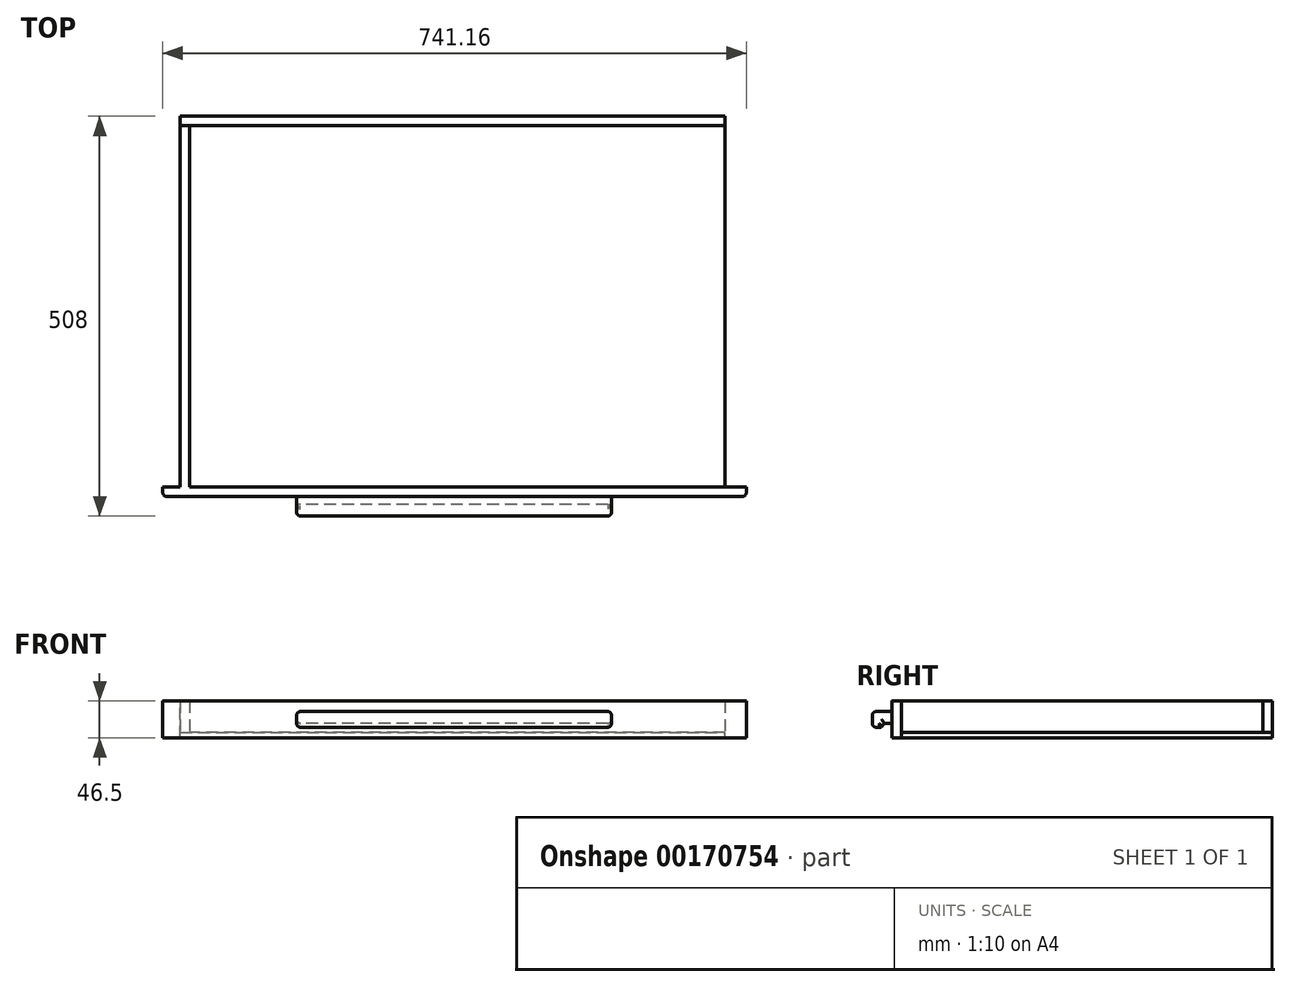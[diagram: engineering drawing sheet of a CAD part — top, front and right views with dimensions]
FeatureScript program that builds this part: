
annotation { "Feature Type Name" : "Feature", "Feature Type Description" : "" }
export const myFeature = defineFeature(function(context is Context, id is Id, definition is map)
    precondition{}
    {
        {
            assignVariable(context, id + "F0", {"name" : "height", "anyValue" : 50});
        }
        {
            var Q0;
            Q0=qCreatedBy(makeId("Top.planeOp"),FACE);
            var sketch = newSketch(context, id + "F1", { "sketchPlane" : qUnion([Q0])});
            skLineSegment(sketch, "E0.bottom", {"start": v(370, -278.25) * mm, "end": v(-370, -278.25) * mm});
            skLineSegment(sketch, "E0.top", {"start": v(370, 209.75) * mm, "end": v(-370, 209.75) * mm});
            skLineSegment(sketch, "E0.left", {"start": v(370, -278.25) * mm, "end": v(370, 209.75) * mm});
            skLineSegment(sketch, "E0.right", {"start": v(-370, -278.25) * mm, "end": v(-370, 209.75) * mm});
            skPoint(sketch, "E0.middle", {"position": v(0, -34.25) * mm});
            skLineSegment(sketch, "E1", {"start": v(-370, 197.75) * mm, "end": v(370, 197.75) * mm});
            skLineSegment(sketch, "E2", {"start": v(-358, 197.75) * mm, "end": v(-358, -278.25) * mm});
            skLineSegment(sketch, "E3.MirrorCS", {"start": v(354.04, 209.75) * mm, "end": v(354.04, -278.25) * mm});
            skLineSegment(sketch, "E4.bottom", {"start": v(-348, -278.25) * mm, "end": v(344.04, -278.25) * mm});
            skLineSegment(sketch, "E4.top", {"start": v(-348, 192.75) * mm, "end": v(344.04, 192.75) * mm});
            skLineSegment(sketch, "E4.left", {"start": v(-348, -278.25) * mm, "end": v(-348, 192.75) * mm});
            skLineSegment(sketch, "E4.right", {"start": v(344.04, -278.25) * mm, "end": v(344.04, 192.75) * mm});
            skLineSegment(sketch, "E5", {"start": v(-348, 180.75) * mm, "end": v(344.04, 180.75) * mm});
            skLineSegment(sketch, "E6", {"start": v(-336, 180.75) * mm, "end": v(-336, -278.25) * mm});
            skLineSegment(sketch, "E7", {"start": v(332.04, 180.75) * mm, "end": v(332.04, -278.25) * mm});
            skLineSegment(sketch, "E8.bottom", {"start": v(-370, -278.25) * mm, "end": v(371.16, -278.25) * mm});
            skLineSegment(sketch, "E8.top", {"start": v(-370, -290.25) * mm, "end": v(371.16, -290.25) * mm});
            skLineSegment(sketch, "E8.left", {"start": v(-370, -278.25) * mm, "end": v(-370, -290.25) * mm});
            skLineSegment(sketch, "E8.right", {"start": v(371.16, -278.25) * mm, "end": v(371.16, -290.25) * mm});
            skSolve(sketch);
        }
        {
            var Q0;
            {var subQ5=sQuery(id+"F1.wireOp",EDGE,"E6");Q0=makeQuery(id+"F1.imprint","IMPRINT",FACE,{"disambiguationData":[TD([[makeQuery(id+"F1.imprint","IMPRINT",EDGE,{"derivedFrom":subQ5}),-1.0]])]});}
            var Q1;
            {var subQ5=sQuery(id+"F1.wireOp",EDGE,"E4.top");Q1=makeQuery(id+"F1.imprint","IMPRINT",FACE,{"disambiguationData":[TD([[makeQuery(id+"F1.imprint","IMPRINT",EDGE,{"derivedFrom":subQ5}),-1.0]])]});}
            var Q2;
            {var subQ0=sQuery(id+"F1.wireOp",EDGE,"E6");Q2=makeQuery(id+"F1.imprint","IMPRINT",FACE,{"disambiguationData":[TD([[makeQuery(id+"F1.imprint","IMPRINT",EDGE,{"derivedFrom":subQ0}),1.0]])]});}
            var Q3;
            {var subQ5=sQuery(id+"F1.wireOp",EDGE,"E7");Q3=makeQuery(id+"F1.imprint","IMPRINT",FACE,{"disambiguationData":[TD([[makeQuery(id+"F1.imprint","IMPRINT",EDGE,{"derivedFrom":subQ5}),1.0]])]});}
            extrude(context, id + "F2", {"entities" : qUnion([Q0, Q1, Q2, Q3]), "oppositeDirection" : true, "depth" : 6.5 * mm});
        }
        {
            var Q0;
            {var subQ5=sQuery(id+"F1.wireOp",EDGE,"E6");Q0=makeQuery(id+"F1.imprint","IMPRINT",FACE,{"disambiguationData":[TD([[makeQuery(id+"F1.imprint","IMPRINT",EDGE,{"derivedFrom":subQ5}),-1.0]])]});}
            extrude(context, id + "F3", {"entities" : qUnion([Q0]), "depth" : (getVariable(context, 'height') - 10) * mm});
        }
        {
            var Q0;
            {var subQ5=sQuery(id+"F1.wireOp",EDGE,"E4.top");Q0=makeQuery(id+"F1.imprint","IMPRINT",FACE,{"disambiguationData":[TD([[makeQuery(id+"F1.imprint","IMPRINT",EDGE,{"derivedFrom":subQ5}),-1.0]])]});}
            var Q1;
            Q1=makeQuery(id+"F3.opExtrude","CAP_FACE",FACE,{"disambiguationData":[OSD([sQuery(id+"F1.wireOp",EDGE,"E4.left"),sQuery(id+"F1.wireOp",EDGE,"E5"),sQuery(id+"F1.wireOp",EDGE,"E6"),sQuery(id+"F1.wireOp",EDGE,"E8.bottom")])],"isStart":false});
            extrude(context, id + "F4", {"entities" : qUnion([Q0]), "endBound" : BoundingType.UP_TO_SURFACE, "endBoundEntityFace" : qUnion([Q1]), "depth" : 25 * mm});
        }
        {
            var Q0;
            Q0=makeQuery(id+"F1.imprint","IMPRINT",FACE,{"disambiguationData":[TD([[makeQuery(id+"F1.imprint","IMPRINT",EDGE,{"derivedFrom":sQuery(id+"F1.wireOp",EDGE,"E8.top")}),1.0]])]});
            var Q1;
            Q1=makeQuery(id+"F3.opExtrude","CAP_FACE",FACE,{"disambiguationData":[OSD([sQuery(id+"F1.wireOp",EDGE,"E4.left"),sQuery(id+"F1.wireOp",EDGE,"E5"),sQuery(id+"F1.wireOp",EDGE,"E6"),sQuery(id+"F1.wireOp",EDGE,"E8.bottom")])],"isStart":false});
            extrude(context, id + "F5", {"entities" : qUnion([Q0]), "endBound" : BoundingType.UP_TO_SURFACE, "endBoundEntityFace" : qUnion([Q1]), "depth" : 25 * mm});
        }
        {
            var Q0;
            Q0=makeQuery(id+"F1.imprint","IMPRINT",FACE,{"disambiguationData":[TD([[makeQuery(id+"F1.imprint","IMPRINT",EDGE,{"derivedFrom":sQuery(id+"F1.wireOp",EDGE,"E8.top")}),1.0]])]});
            var Q1;
            Q1=makeQuery(id+"F2.opExtrude","CAP_FACE",FACE,{"disambiguationData":[OSD([sQuery(id+"F1.wireOp",EDGE,"E4.top"),sQuery(id+"F1.wireOp",EDGE,"E4.left"),sQuery(id+"F1.wireOp",EDGE,"E4.right"),sQuery(id+"F1.wireOp",EDGE,"E8.bottom")])],"isStart":false});
            extrude(context, id + "F6", {"entities" : qUnion([Q0]), "operationType" : NewBodyOperationType.ADD, "endBound" : BoundingType.UP_TO_SURFACE, "oppositeDirection" : true, "endBoundEntityFace" : qUnion([Q1]), "depth" : 25 * mm});
        }
        {
            var Q0;
            Q0=qCreatedBy(makeId("Right.planeOp"),FACE);
            var sketch = newSketch(context, id + "F7", { "sketchPlane" : qUnion([Q0])});
            skLineSegment(sketch, "E9.0.1", {"start": v(-290.25, 40) * mm, "end": v(-290.25, -6.5) * mm});
            skLineSegment(sketch, "E9.0.3", {"start": v(-290.25, -6.5) * mm, "end": v(-290.25, 40) * mm});
            skLineSegment(sketch, "E10.bottom", {"start": v(-290.25, 26.69) * mm, "end": v(-310.25, 26.69) * mm});
            skLineSegment(sketch, "E10.top", {"start": v(-305.31, 6.69) * mm, "end": v(-310.25, 6.69) * mm});
            skLineSegment(sketch, "E10.left", {"start": v(-290.25, 26.69) * mm, "end": v(-290.25, 6.69) * mm});
            skLineSegment(sketch, "E10.right", {"start": v(-315.25, 21.69) * mm, "end": v(-315.25, 11.69) * mm});
            skPoint(sketch, "E11.visualSharp", {"position": v(-315.25, 26.69) * mm});
            skArc(sketch, "E11.filletArc", {"start": v(-310.25, 26.69) * mm, "mid": v(-313.79, 25.22) * mm, "end": v(-315.25, 21.69) * mm});
            skPoint(sketch, "E12.visualSharp", {"position": v(-315.25, 6.69) * mm});
            skArc(sketch, "E12.filletArc", {"start": v(-315.25, 11.69) * mm, "mid": v(-313.79, 8.15) * mm, "end": v(-310.25, 6.69) * mm});
            skLineSegment(sketch, "E13", {"start": v(-290.25, 11.69) * mm, "end": v(-300.25, 11.69) * mm});
            skLineSegment(sketch, "E14", {"start": v(-300.25, 11.69) * mm, "end": v(-302.86, 7.97) * mm});
            skPoint(sketch, "E15.visualSharp", {"position": v(-303.75, 6.69) * mm});
            skArc(sketch, "E15.filletArc", {"start": v(-305.31, 6.69) * mm, "mid": v(-303.93, 7.03) * mm, "end": v(-302.86, 7.97) * mm});
            skSolve(sketch);
        }
        {
            var Q0;
            {var subQ2=sQuery(id+"F7.wireOp",EDGE,"E10.bottom");Q0=makeQuery(id+"F7.imprint","IMPRINT",FACE,{"disambiguationData":[TD([[makeQuery(id+"F7.imprint","IMPRINT",EDGE,{"derivedFrom":subQ2}),1.0]])]});}
            extrude(context, id + "F8", {"entities" : qUnion([Q0]), "endBound" : BoundingType.SYMMETRIC, "depth" : 400 * mm});
        }
        {
            var Q0;
            Q0=makeQuery(id+"F8.opExtrude","CAP_EDGE",EDGE,{"disambiguationData":[OSD([sQuery(id+"F7.wireOp",EDGE,"E10.right")])],"isStart":false});
            var Q1;
            Q1=makeQuery(id+"F8.opExtrude","CAP_EDGE",EDGE,{"disambiguationData":[OSD([sQuery(id+"F7.wireOp",EDGE,"E13")])],"isStart":false});
            var Q2;
            Q2=makeQuery(id+"F8.opExtrude","CAP_EDGE",EDGE,{"disambiguationData":[OSD([sQuery(id+"F7.wireOp",EDGE,"E10.right")])],"isStart":true});
            var Q3;
            Q3=makeQuery(id+"F8.opExtrude","CAP_EDGE",EDGE,{"disambiguationData":[OSD([sQuery(id+"F7.wireOp",EDGE,"E13")])],"isStart":true});
            fillet(context, id + "F9", {"entities" : qUnion([Q0, Q1, Q2, Q3]), "radius" : 5 * mm, "tangentPropagation" : true, "allowEdgeOverflow" : false});
        }
        {
            var Q0;
            {var subQ0=sQuery(id+"F1.wireOp",EDGE,"E8.right");var subQ1=sQuery(id+"F1.wireOp",EDGE,"E8.top");Q0=makeQuery(id+"F6.boolean.opBoolean","MERGE",EDGE,{"derivedFrom":[makeQuery(id+"F5.opExtrude","SWEPT_EDGE",EDGE,{"disambiguationData":[OSD([subQ1,subQ0])]}),makeQuery(id+"F6.opExtrude","SWEPT_EDGE",EDGE,{"disambiguationData":[OSD([subQ1,subQ0])]})]});}
            var Q1;
            {var subQ0=sQuery(id+"F1.wireOp",EDGE,"E8.left");var subQ1=sQuery(id+"F1.wireOp",EDGE,"E8.top");Q1=makeQuery(id+"F6.boolean.opBoolean","MERGE",EDGE,{"derivedFrom":[makeQuery(id+"F5.opExtrude","SWEPT_EDGE",EDGE,{"disambiguationData":[OSD([subQ1,subQ0])]}),makeQuery(id+"F6.opExtrude","SWEPT_EDGE",EDGE,{"disambiguationData":[OSD([subQ1,subQ0])]})]});}
            fillet(context, id + "F10", {"entities" : qUnion([Q0, Q1]), "radius" : 5 * mm, "tangentPropagation" : true, "allowEdgeOverflow" : false});
        }
    });
